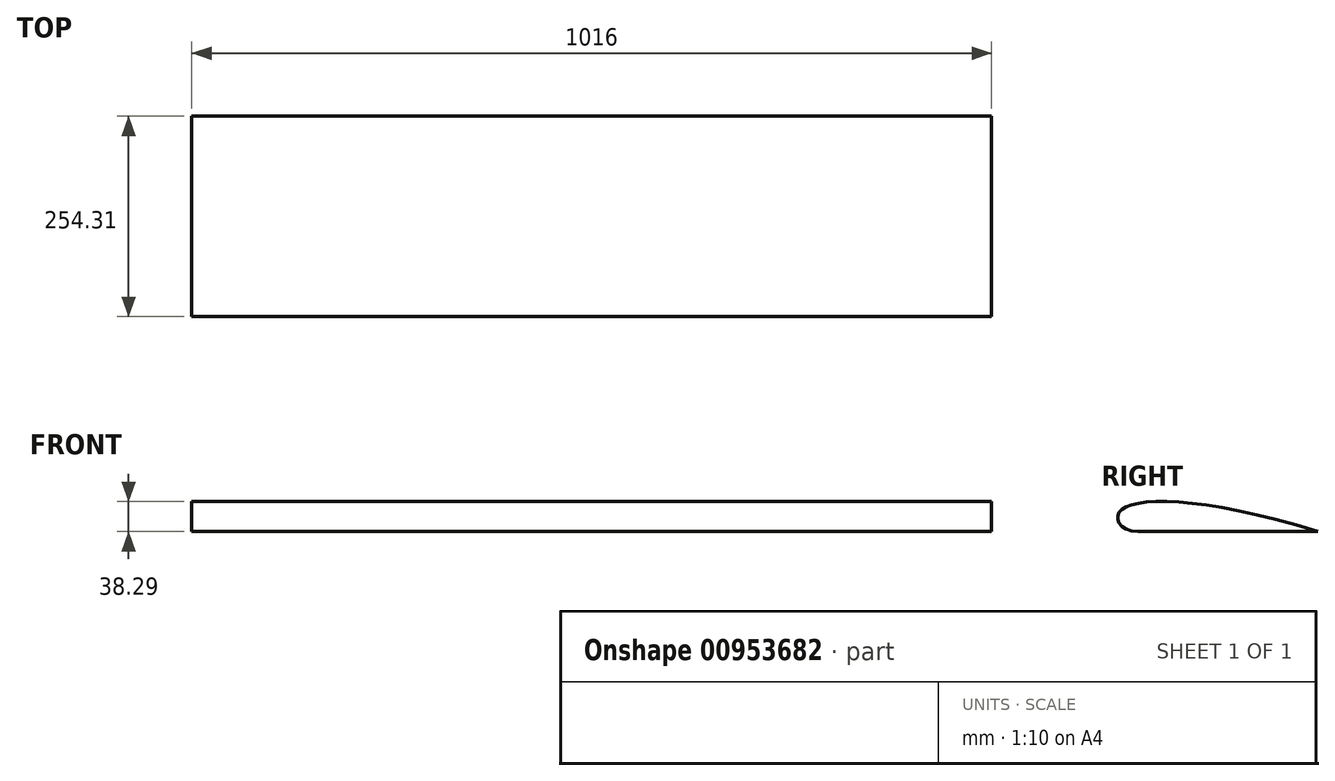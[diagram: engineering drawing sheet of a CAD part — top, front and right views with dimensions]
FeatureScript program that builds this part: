
annotation { "Feature Type Name" : "Feature", "Feature Type Description" : "" }
export const myFeature = defineFeature(function(context is Context, id is Id, definition is map)
    precondition{}
    {
        {
            var Q0;
            Q0=qCreatedBy(makeId("Right.planeOp"),FACE);
            var sketch = newSketch(context, id + "F0", { "sketchPlane" : qUnion([Q0])});
            skFitSpline(sketch, "E0", {"points": [v(25.88, 0) * mm, v(0, 20.4) * mm, v(254, 0) * mm], "startDerivative": vector(-216.66, 0) * mm, "endDerivative": vector(640.95, -201.15) * mm});
            skLineSegment(sketch, "E1", {"start": v(25.88, 0) * mm, "end": v(254, 0) * mm});
            skSolve(sketch);
        }
        {
            var Q0;
            Q0=makeQuery(id+"F0.imprint","IMPRINT",FACE,{"disambiguationData":[TD([[makeQuery(id+"F0.imprint","IMPRINT",EDGE,{"derivedFrom":sQuery(id+"F0.wireOp",EDGE,"E0")}),-1.0]])]});
            extrude(context, id + "F1", {"entities" : qUnion([Q0]), "depth" : 1016 * mm, "offsetDistance" : 25.4 * mm});
        }
    });
